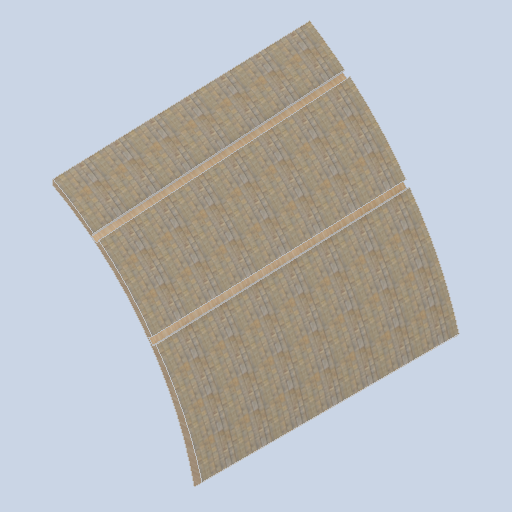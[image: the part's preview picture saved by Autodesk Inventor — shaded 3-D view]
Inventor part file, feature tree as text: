
AUTODESK INVENTOR PART (.ipt)
format: ipt  version: 2024.2 (Build 282272000, 272)  size: 361,984 bytes
history: native  units: in
note: dims shown in document units (in); Inventor stores cm internally (conversion verified against a paired STEP export)
features: other x3, sketch x2, plane x2
ambient origin geometry x8: Origin, YZ Plane, XZ Plane, XY Plane, X Axis, Y Axis, Z Axis, Center Point
bodies: Solid1 (feature_tree)
feature tree (7):
  other  "panel_block_03_MIR.ipt"
  other  "Solid1::panel_block_03_MIR.ipt"
  other  "TaggingFeature1"
  sketch  "Sketch1"  dims[d0=0.3937in]
  sketch  "Sketch2"
  plane  "Work Plane1"
  plane  "Work Plane2"
